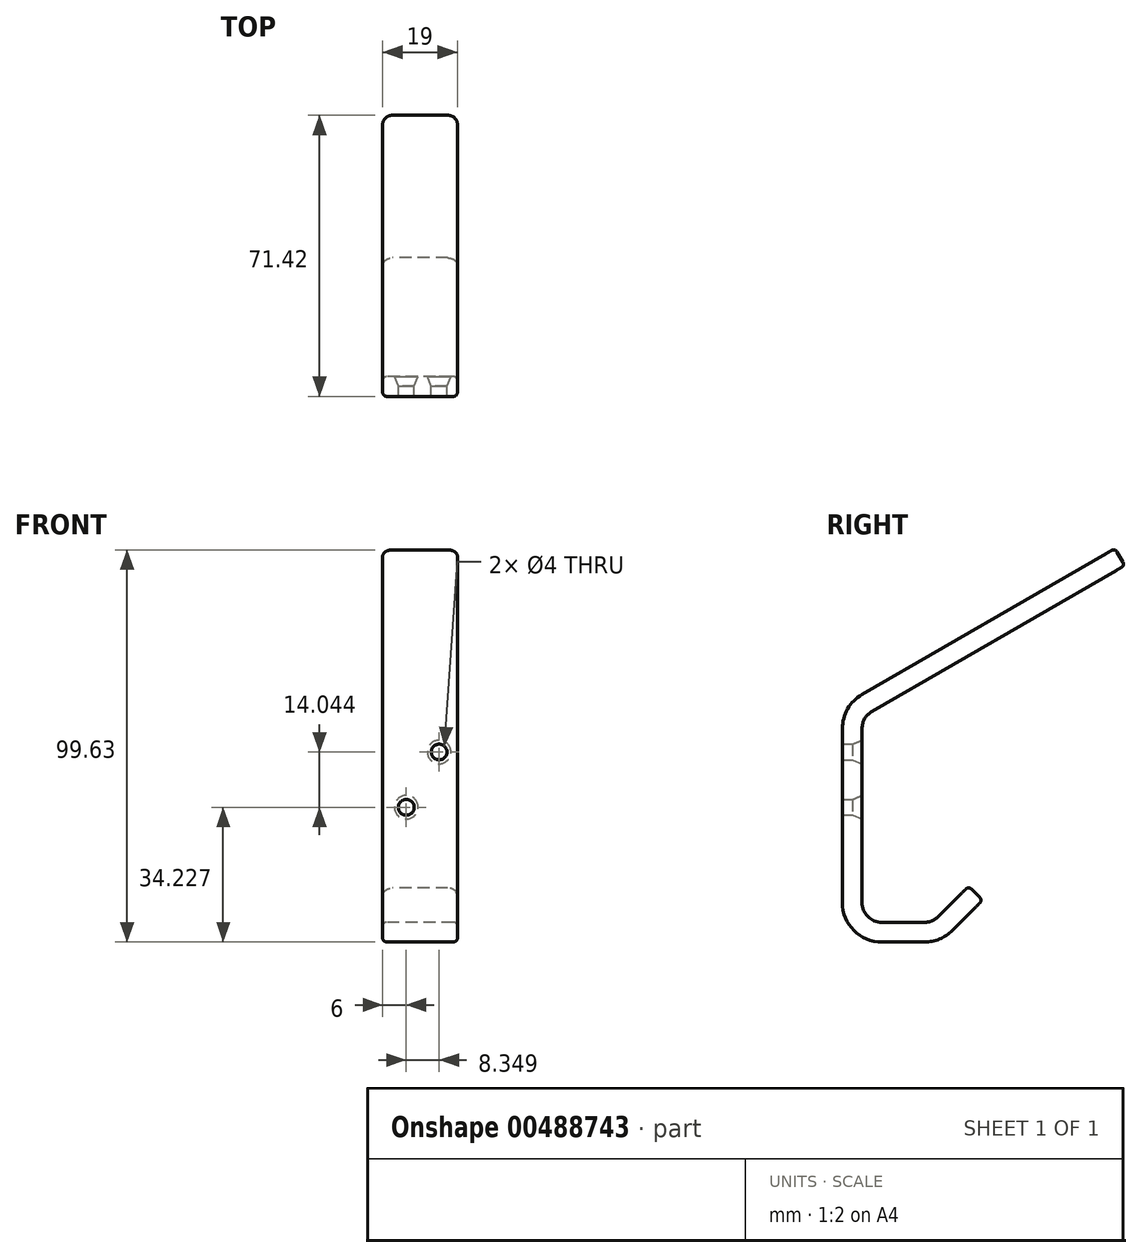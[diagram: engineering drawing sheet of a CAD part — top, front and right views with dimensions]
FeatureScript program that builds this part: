
annotation { "Feature Type Name" : "Feature", "Feature Type Description" : "" }
export const myFeature = defineFeature(function(context is Context, id is Id, definition is map)
    precondition{}
    {
        {
            var Q0;
            Q0=qCreatedBy(makeId("Right.planeOp"),FACE);
            var sketch = newSketch(context, id + "F0", { "sketchPlane" : qUnion([Q0])});
            skLineSegment(sketch, "E0", {"start": v(0, 0) * mm, "end": v(0, 60) * mm});
            skLineSegment(sketch, "E1", {"start": v(0, 60) * mm, "end": v(69.28, 100) * mm});
            skLineSegment(sketch, "E2", {"start": v(25, 0) * mm, "end": v(35.6, 10.6) * mm});
            skLineSegment(sketch, "E3", {"start": v(35.6, 10.6) * mm, "end": v(32.07, 14.14) * mm});
            skLineSegment(sketch, "E4", {"start": v(5, 5) * mm, "end": v(22.93, 5) * mm});
            skPoint(sketch, "E5.start.orphan", {"position": v(-21.74, 0) * mm});
            skLineSegment(sketch, "E6", {"start": v(5, 5) * mm, "end": v(5, 57.11) * mm});
            skLineSegment(sketch, "E7", {"start": v(0, 0) * mm, "end": v(25, 0) * mm});
            skLineSegment(sketch, "E8", {"start": v(32.07, 14.14) * mm, "end": v(22.93, 5) * mm});
            skLineSegment(sketch, "E9", {"start": v(69.28, 100) * mm, "end": v(71.78, 95.67) * mm});
            skLineSegment(sketch, "E10", {"start": v(71.78, 95.67) * mm, "end": v(5, 57.11) * mm});
            skSolve(sketch);
        }
        {
            var Q0;
            Q0 = qSketchRegion(id + "F0", true);
            extrude(context, id + "F1", {"entities" : qUnion([Q0]), "depth" : 19 * mm, "offsetDistance" : 25 * mm});
        }
        {
            var Q0;
            Q0=makeQuery(id+"F1.opExtrude","SWEPT_EDGE",EDGE,{"disambiguationData":[OSD([sQuery(id+"F0.wireOp",EDGE,"E0"),sQuery(id+"F0.wireOp",EDGE,"E1")])]});
            fillet(context, id + "F2", {"entities" : qUnion([Q0]), "radius" : 10 * mm, "tangentPropagation" : true, "allowEdgeOverflow" : false});
        }
        {
            var Q0;
            Q0=makeQuery(id+"F1.opExtrude","SWEPT_EDGE",EDGE,{"disambiguationData":[OSD([sQuery(id+"F0.wireOp",EDGE,"E0"),sQuery(id+"F0.wireOp",EDGE,"E7")])]});
            fillet(context, id + "F3", {"entities" : qUnion([Q0]), "radius" : 10 * mm, "tangentPropagation" : true, "allowEdgeOverflow" : false});
        }
        {
            var Q0;
            Q0=makeQuery(id+"F1.opExtrude","SWEPT_EDGE",EDGE,{"disambiguationData":[OSD([sQuery(id+"F0.wireOp",EDGE,"E4"),sQuery(id+"F0.wireOp",EDGE,"E6")])]});
            fillet(context, id + "F4", {"entities" : qUnion([Q0]), "radius" : 5 * mm, "tangentPropagation" : true, "allowEdgeOverflow" : false});
        }
        {
            var Q0;
            Q0=makeQuery(id+"F1.opExtrude","SWEPT_EDGE",EDGE,{"disambiguationData":[OSD([sQuery(id+"F0.wireOp",EDGE,"E6"),sQuery(id+"F0.wireOp",EDGE,"E10")])]});
            fillet(context, id + "F5", {"entities" : qUnion([Q0]), "radius" : 5 * mm, "tangentPropagation" : true, "allowEdgeOverflow" : false});
        }
        {
            var Q0;
            Q0=makeQuery(id+"F1.opExtrude","SWEPT_EDGE",EDGE,{"disambiguationData":[OSD([sQuery(id+"F0.wireOp",EDGE,"E2"),sQuery(id+"F0.wireOp",EDGE,"E7")])]});
            fillet(context, id + "F6", {"entities" : qUnion([Q0]), "radius" : 10 * mm, "tangentPropagation" : true, "allowEdgeOverflow" : false});
        }
        {
            var Q0;
            Q0=makeQuery(id+"F1.opExtrude","SWEPT_EDGE",EDGE,{"disambiguationData":[OSD([sQuery(id+"F0.wireOp",EDGE,"E4"),sQuery(id+"F0.wireOp",EDGE,"E8")])]});
            fillet(context, id + "F7", {"entities" : qUnion([Q0]), "radius" : 5 * mm, "tangentPropagation" : true, "allowEdgeOverflow" : false});
        }
        {
            var Q0;
            Q0=makeQuery(id+"F1.opExtrude","CAP_EDGE",EDGE,{"disambiguationData":[OSD([sQuery(id+"F0.wireOp",EDGE,"E3")])],"isStart":false});
            var Q1;
            Q1=makeQuery(id+"F1.opExtrude","CAP_EDGE",EDGE,{"disambiguationData":[OSD([sQuery(id+"F0.wireOp",EDGE,"E3")])],"isStart":true});
            var Q2;
            Q2=makeQuery(id+"F1.opExtrude","CAP_EDGE",EDGE,{"disambiguationData":[OSD([sQuery(id+"F0.wireOp",EDGE,"E9")])],"isStart":true});
            var Q3;
            Q3=makeQuery(id+"F1.opExtrude","CAP_EDGE",EDGE,{"disambiguationData":[OSD([sQuery(id+"F0.wireOp",EDGE,"E9")])],"isStart":false});
            fillet(context, id + "F8", {"entities" : qUnion([Q0, Q1, Q2, Q3]), "radius" : 2.5 * mm, "tangentPropagation" : true, "allowEdgeOverflow" : false});
        }
        {
            var Q0;
            Q0=makeQuery(id+"F1.opExtrude","SWEPT_EDGE",EDGE,{"disambiguationData":[OSD([sQuery(id+"F0.wireOp",EDGE,"E2"),sQuery(id+"F0.wireOp",EDGE,"E3")])]});
            var Q1;
            Q1=makeQuery(id+"F1.opExtrude","SWEPT_EDGE",EDGE,{"disambiguationData":[OSD([sQuery(id+"F0.wireOp",EDGE,"E3"),sQuery(id+"F0.wireOp",EDGE,"E8")])]});
            fillet(context, id + "F9", {"entities" : qUnion([Q0, Q1]), "radius" : 1 * mm, "tangentPropagation" : true, "allowEdgeOverflow" : false});
        }
        {
            var Q0;
            Q0=makeQuery(id+"F1.opExtrude","SWEPT_FACE",FACE,{"disambiguationData":[OSD([sQuery(id+"F0.wireOp",EDGE,"E6")])]});
            var sketch = newSketch(context, id + "F10", { "sketchPlane" : qUnion([Q0])});
            skPoint(sketch, "E11", {"position": v(-14.35, 48.27) * mm});
            skLineSegment(sketch, "E12", {"start": v(-1, 34.23) * mm, "end": v(-6, 34.23) * mm});
            skSolve(sketch);
        }
        {
            var Q0;
            Q0=sQuery(id+"F10.wireOp",VERTEX,"E11");
            var Q1;
            Q1=makeQuery(id+"F1.opExtrude","SWEPT_BODY",BODY,{"disambiguationData":[OSD([sQuery(id+"F0.wireOp",EDGE,"E0"),sQuery(id+"F0.wireOp",EDGE,"E1"),sQuery(id+"F0.wireOp",EDGE,"E2"),sQuery(id+"F0.wireOp",EDGE,"E3"),sQuery(id+"F0.wireOp",EDGE,"E4"),sQuery(id+"F0.wireOp",EDGE,"E6"),sQuery(id+"F0.wireOp",EDGE,"E7"),sQuery(id+"F0.wireOp",EDGE,"E8"),sQuery(id+"F0.wireOp",EDGE,"E9"),sQuery(id+"F0.wireOp",EDGE,"E10")])]});
            hole(context, id + "F11", {"style" : HoleStyle.C_SINK, "endStyle" : HoleEndStyle.THROUGH, "holeDiameter" : 4 * mm, "cSinkDiameter" : 6 * mm, "cSinkAngle" : 45 * degree, "isTappedThrough" : true, "tappedDepth" : 12 * mm, "tapClearance" : 3, "locations" : qUnion([Q0]), "scope" : qUnion([Q1])});
        }
        {
            var Q0;
            Q0=sQuery(id+"F10.wireOp",VERTEX,"E12.end");
            var Q1;
            Q1=makeQuery(id+"F1.opExtrude","SWEPT_BODY",BODY,{"disambiguationData":[OSD([sQuery(id+"F0.wireOp",EDGE,"E0"),sQuery(id+"F0.wireOp",EDGE,"E1"),sQuery(id+"F0.wireOp",EDGE,"E2"),sQuery(id+"F0.wireOp",EDGE,"E3"),sQuery(id+"F0.wireOp",EDGE,"E4"),sQuery(id+"F0.wireOp",EDGE,"E6"),sQuery(id+"F0.wireOp",EDGE,"E7"),sQuery(id+"F0.wireOp",EDGE,"E8"),sQuery(id+"F0.wireOp",EDGE,"E9"),sQuery(id+"F0.wireOp",EDGE,"E10")])]});
            hole(context, id + "F12", {"style" : HoleStyle.C_SINK, "endStyle" : HoleEndStyle.THROUGH, "holeDiameter" : 4 * mm, "cSinkDiameter" : 6 * mm, "cSinkAngle" : 45 * degree, "isTappedThrough" : true, "tappedDepth" : 12 * mm, "tapClearance" : 3, "locations" : qUnion([Q0]), "scope" : qUnion([Q1])});
        }
    });
